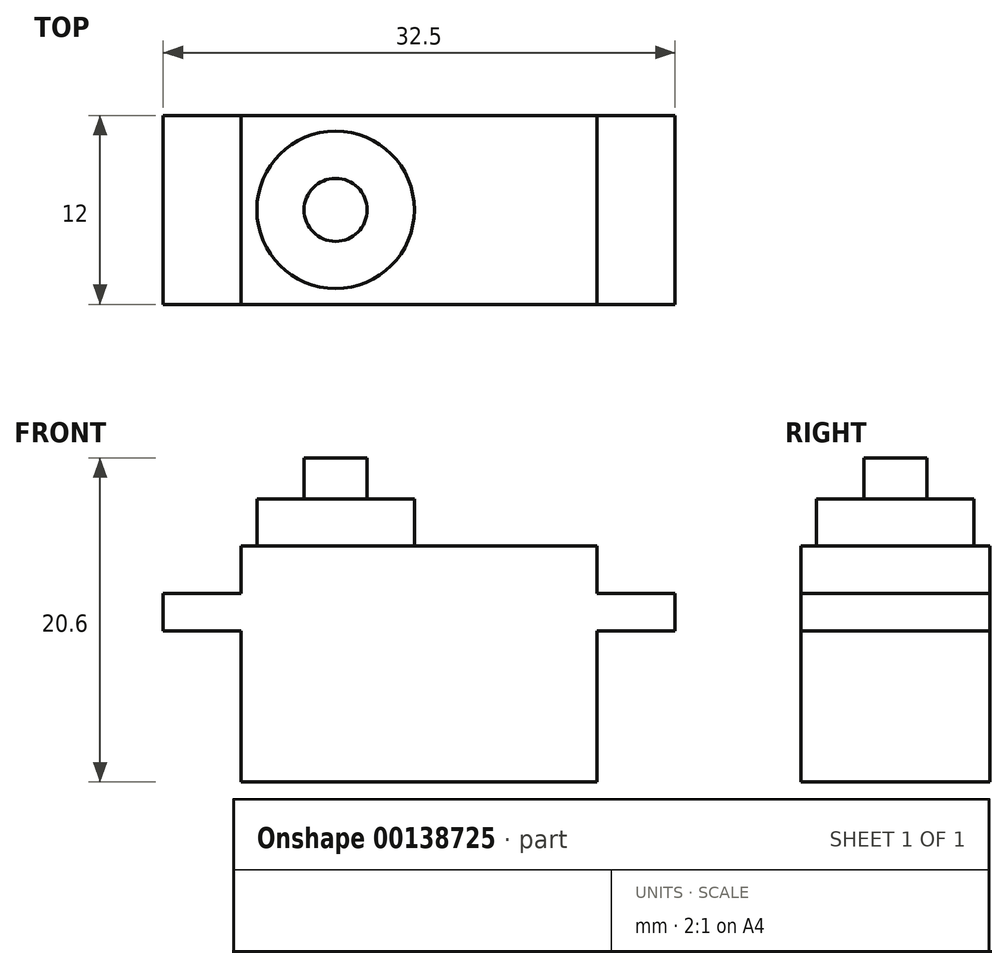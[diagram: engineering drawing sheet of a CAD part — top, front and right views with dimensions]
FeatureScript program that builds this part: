
annotation { "Feature Type Name" : "Feature", "Feature Type Description" : "" }
export const myFeature = defineFeature(function(context is Context, id is Id, definition is map)
    precondition{}
    {
        {
            var Q0;
            Q0=qCreatedBy(makeId("Top.planeOp"),FACE);
            var sketch = newSketch(context, id + "F0", { "sketchPlane" : qUnion([Q0])});
            skPoint(sketch, "E0", {"position": v(-10.95, 0) * mm});
            skPoint(sketch, "E1", {"position": v(21.55, 0) * mm});
            skPoint(sketch, "E2", {"position": v(0, 6) * mm});
            skPoint(sketch, "E3", {"position": v(0, -6) * mm});
            skLineSegment(sketch, "E4.bottom", {"start": v(-10.95, 6) * mm, "end": v(21.55, 6) * mm});
            skLineSegment(sketch, "E4.top", {"start": v(-10.95, -6) * mm, "end": v(21.55, -6) * mm});
            skLineSegment(sketch, "E4.left", {"start": v(-10.95, 6) * mm, "end": v(-10.95, -6) * mm});
            skLineSegment(sketch, "E4.right", {"start": v(21.55, 6) * mm, "end": v(21.55, -6) * mm});
            skSolve(sketch);
        }
        {
            var Q0;
            Q0 = qSketchRegion(id + "F0", true);
            extrude(context, id + "F1", {"entities" : qUnion([Q0]), "depth" : 2.4 * mm});
        }
        {
            var Q0;
            Q0=makeQuery(id+"F1.opExtrude","CAP_FACE",FACE,{"disambiguationData":[OSD([sQuery(id+"F0.wireOp",EDGE,"E4.bottom"),sQuery(id+"F0.wireOp",EDGE,"E4.top"),sQuery(id+"F0.wireOp",EDGE,"E4.left"),sQuery(id+"F0.wireOp",EDGE,"E4.right")])],"isStart":false});
            var sketch = newSketch(context, id + "F2", { "sketchPlane" : qUnion([Q0])});
            skPoint(sketch, "E5", {"position": v(-6, 0) * mm});
            skPoint(sketch, "E6", {"position": v(16.6, 0) * mm});
            skPoint(sketch, "E7.0", {"position": v(-10.95, 6) * mm});
            skPoint(sketch, "E8.0", {"position": v(21.55, -6) * mm});
            skLineSegment(sketch, "E9.bottom", {"start": v(-6, 6) * mm, "end": v(16.6, 6) * mm});
            skLineSegment(sketch, "E9.top", {"start": v(-6, -6) * mm, "end": v(16.6, -6) * mm});
            skLineSegment(sketch, "E9.left", {"start": v(-6, 6) * mm, "end": v(-6, -6) * mm});
            skLineSegment(sketch, "E9.right", {"start": v(16.6, 6) * mm, "end": v(16.6, -6) * mm});
            skSolve(sketch);
        }
        {
            var Q0;
            Q0 = qSketchRegion(id + "F2", true);
            extrude(context, id + "F3", {"entities" : qUnion([Q0]), "operationType" : NewBodyOperationType.ADD, "depth" : 3 * mm, "hasSecondDirection" : true, "secondDirectionOppositeDirection" : true, "secondDirectionDepth" : 12 * mm});
        }
        {
            var Q0;
            Q0=makeQuery(id+"F3.opExtrude","CAP_FACE",FACE,{"disambiguationData":[OSD([sQuery(id+"F2.wireOp",EDGE,"E9.bottom"),sQuery(id+"F2.wireOp",EDGE,"E9.top"),sQuery(id+"F2.wireOp",EDGE,"E9.left"),sQuery(id+"F2.wireOp",EDGE,"E9.right")])],"isStart":false});
            var sketch = newSketch(context, id + "F4", { "sketchPlane" : qUnion([Q0])});
            skCircle(sketch, "E10", {"center": v(0, 0) * mm, "radius": 5 * mm});
            skSolve(sketch);
        }
        {
            var Q0;
            Q0 = qSketchRegion(id + "F4", true);
            extrude(context, id + "F5", {"entities" : qUnion([Q0]), "operationType" : NewBodyOperationType.ADD, "depth" : 3 * mm});
        }
        {
            var Q0;
            Q0=makeQuery(id+"F5.opExtrude","CAP_FACE",FACE,{"disambiguationData":[OSD([sQuery(id+"F4.wireOp",EDGE,"E10")])],"isStart":false});
            var sketch = newSketch(context, id + "F6", { "sketchPlane" : qUnion([Q0])});
            skCircle(sketch, "E11", {"center": v(0, 0) * mm, "radius": 2 * mm});
            skSolve(sketch);
        }
        {
            var Q0;
            Q0 = qSketchRegion(id + "F6", true);
            extrude(context, id + "F7", {"entities" : qUnion([Q0]), "operationType" : NewBodyOperationType.ADD, "depth" : 2.6 * mm});
        }
    });
